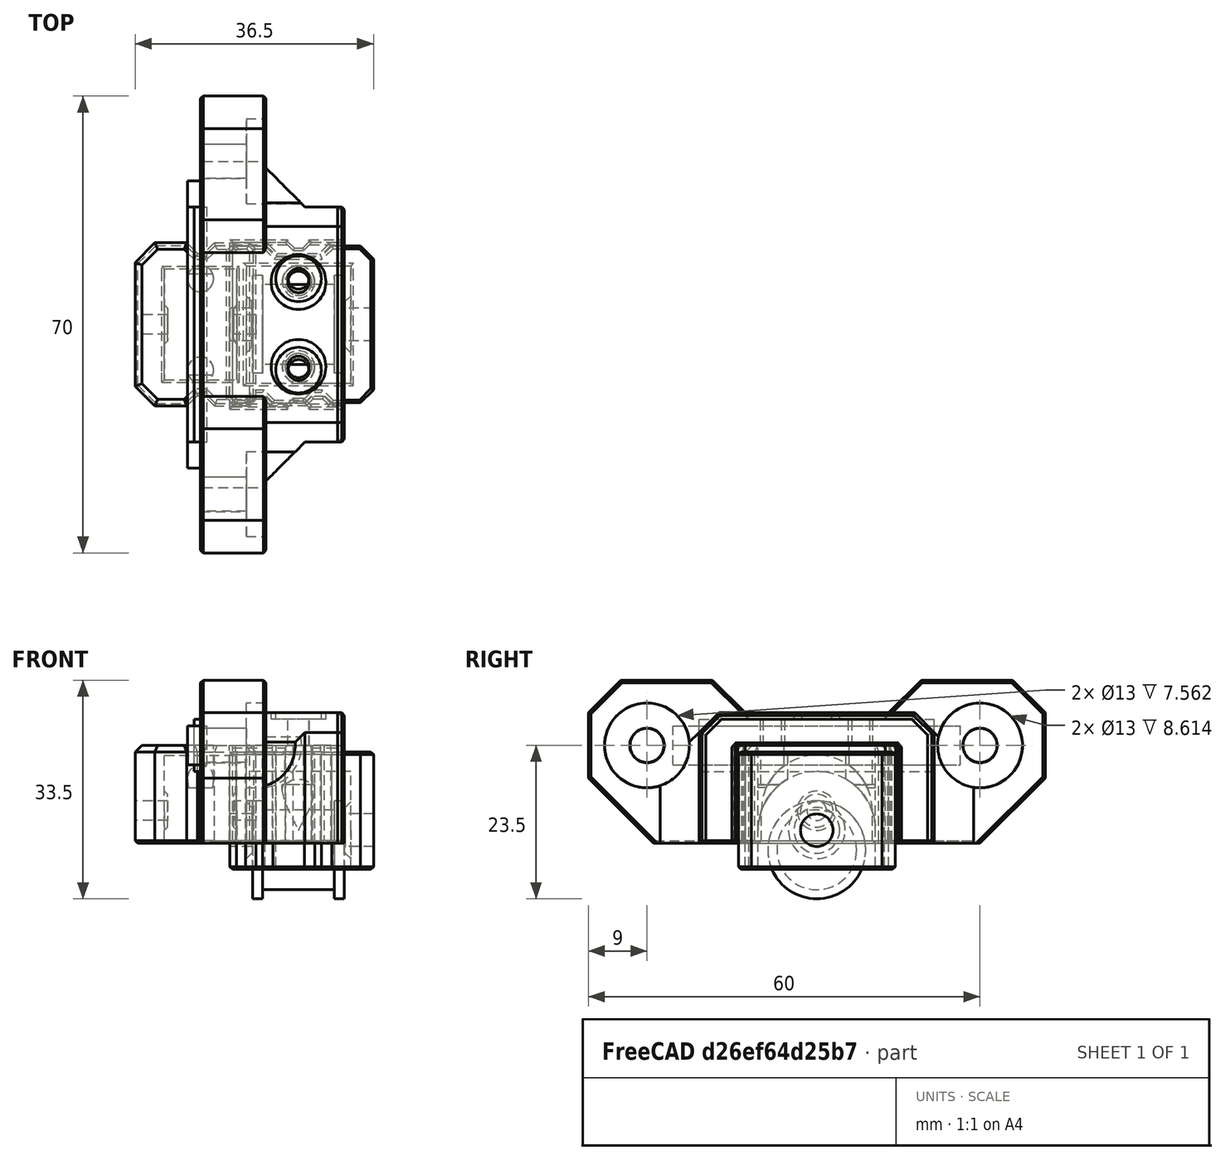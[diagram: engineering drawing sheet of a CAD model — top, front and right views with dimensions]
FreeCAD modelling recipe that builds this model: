
FCSTD DOCUMENT  (FreeCAD 0.18R16146 (Git))
Label: idler-tensioner-9mm
License: All rights reserved
LicenseURL: http://en.wikipedia.org/wiki/All_rights_reserved
objects: Part::Chamfer×38, Part::MultiFuse×33, Part::Cylinder×29, Part::Box×26, Part::Cut×12, Part::Feature×2, App::Part×2
note: 140 computed .brp shape members not serialized (recipe doc carries the construction recipe); baked Part::Feature solids carry a one-line shape summary decoded from their .brp

FEATURE [Part::Box] Box  label="Cube"
  AttacherType = Attacher::AttachEngine3D
  Height = 15
  Length = 18.5
  Placement = pos=(-10,-12.5,0) rot=(0,0,1;0rad)
  Width = 25
FEATURE [Part::Cylinder] Cylinder
  Angle = 360
  AttacherType = Attacher::AttachEngine3D
  Height = 22
  Placement = pos=(11,0,5) rot=(0,-1,0;1.5708rad)
  Radius = 1.5
FEATURE [Part::Cylinder] Cylinder001
  Angle = 360
  AttacherType = Attacher::AttachEngine3D
  Height = 11.1
  Placement = pos=(-5.55,0,5) rot=(0,1,0;1.5708rad)
  Radius = 8.5
FEATURE [Part::Box] Box001  label="Cube001"
  AttacherType = Attacher::AttachEngine3D
  Height = 5
  Length = 11.1
  Placement = pos=(-5.55,-8.5,0) rot=(0,0,1;0rad)
  Width = 17
FEATURE [Part::Cylinder] Cylinder003
  Angle = 360
  AttacherType = Attacher::AttachEngine3D
  Height = 10
  Placement = pos=(0,-7,8.5) rot=(0,0,1;0rad)
  Radius = 2
FEATURE [Part::Box] Box002  label="Cube002"
  AttacherType = Attacher::AttachEngine3D
  Height = 21
  Length = 4.2
  Placement = pos=(-2.1,-21,0) rot=(0,0,1;0rad)
  Width = 10.1
FEATURE [Part::Box] Box003  label="Cube003"
  AttacherType = Attacher::AttachEngine3D
  Height = 21
  Length = 4.2
  Placement = pos=(-2.1,10.9,0) rot=(0,0,1;0rad)
  Width = 10.1
FEATURE [Part::Cylinder] Cylinder004
  Angle = 360
  AttacherType = Attacher::AttachEngine3D
  Height = 1
  Placement = pos=(5.05,0,5) rot=(0,1,0;1.5708rad)
  Radius = 3
FEATURE [Part::Cylinder] Cylinder005
  Angle = 360
  AttacherType = Attacher::AttachEngine3D
  Height = 1
  Placement = pos=(-6.05,0,5) rot=(0,1,0;1.5708rad)
  Radius = 3
FEATURE [Part::Box] Box004  label="Cube004"
  AttacherType = Attacher::AttachEngine3D
  Height = 20
  Length = 22
  Placement = pos=(-15,-18,0) rot=(0,0,1;0rad)
  Width = 36
FEATURE [Part::Box] Box005  label="Cube005"
  AttacherType = Attacher::AttachEngine3D
  Height = 15
  Length = 20.2
  Placement = pos=(-10.1,-12.6,0) rot=(0,0,1;0rad)
  Width = 25.2
FEATURE [Part::Box] Box006  label="Cube006"
  AttacherType = Attacher::AttachEngine3D
  Height = 15
  Length = 4
  Placement = pos=(-2,11.3,0) rot=(0,0,1;0rad)
  Width = 1.7
FEATURE [Part::Box] Box007  label="Cube007"
  AttacherType = Attacher::AttachEngine3D
  Height = 15
  Length = 4
  Placement = pos=(-2,-13,0) rot=(0,0,1;0rad)
  Width = 1.7
FEATURE [Part::Cylinder] Cylinder006
  Angle = 360
  AttacherType = Attacher::AttachEngine3D
  Height = 10
  Placement = pos=(0,0,29) rot=(0,0,1;0rad)
  Radius = 3.5
FEATURE [Part::Cylinder] Cylinder007
  Angle = 360
  AttacherType = Attacher::AttachEngine3D
  Height = 12
  Placement = pos=(0,0,19) rot=(0,0,1;0rad)
  Radius = 1.6
FEATURE [Part::Box] Box008  label="Cube008"
  AttacherType = Attacher::AttachEngine3D
  Height = 6
  Length = 3
  Placement = pos=(-17,-22,12) rot=(0,0,1;0rad)
  Width = 44
FEATURE [Part::MultiFuse] Fusion
  Shapes = -> [Cylinder001,Box001]
FEATURE [Part::Chamfer] Chamfer003008
  Base = -> Box002
  Edges = 2 edges r=1.6: [Edge3,Edge7]
FEATURE [Part::Chamfer] Chamfer003009
  Base = -> Box003
  Edges = 2 edges r=1.6: [Edge1,Edge5]
FEATURE [Part::Cut] Cut
  Base = -> Box
  Tool = -> Fusion
FEATURE [Part::Cylinder] Cylinder008
  Angle = 360
  AttacherType = Attacher::AttachEngine3D
  Height = 10
  Placement = pos=(0,7,8.5) rot=(0,0,1;0rad)
  Radius = 2
FEATURE [Part::MultiFuse] Fusion007
  Shapes = -> [Cylinder003,Cylinder008]
FEATURE [Part::Cut] Cut001001009
  Base = -> Cut
  Tool = -> Fusion007
FEATURE [Part::MultiFuse] Fusion008
  Shapes = -> [Chamfer003008,Chamfer003009]
FEATURE [Part::Cut] Cut001001010
  Base = -> Cut001001009
  Tool = -> Fusion008
FEATURE [Part::Chamfer] Chamfer003010
  Base = -> Cut001001010
  Edges = 2 edges r=3: [Edge1,Edge3]
FEATURE [Part::Chamfer] Chamfer003011
  Base = -> Chamfer003010
  Edges = 2 edges r=1: [Edge48,Edge50]
FEATURE [Part::Chamfer] Chamfer003012
  Base = -> Chamfer003011
  Edges = 16 edges r=1: [Edge1,Edge2,Edge3,Edge4,Edge5,Edge6,Edge7,Edge8,Edge9,Edge10,Edge11,Edge12,Edge13,Edge14,Edge15,Edge16]
FEATURE [Part::Chamfer] Chamfer003015
  Base = -> Chamfer003012
  Edges = 24 edges r=0.4: [Edge60,Edge63,Edge64,Edge66,Edge69,Edge70,Edge72,Edge75,Edge76,Edge79,Edge81,Edge83,Edge84,Edge86,Edge88,Edge90,Edge97,Edge98,Edge99,Edge100,Edge101,Edge102,Edge103,Edge104]
FEATURE [Part::MultiFuse] Fusion011
  Shapes = -> [Box007,Box006]
FEATURE [Part::Chamfer] Chamfer
  Base = -> Fusion011
  Edges = 4 edges r=1.2: [Edge3,Edge7,Edge13,Edge17]
FEATURE [Part::MultiFuse] Fusion013
  Placement = pos=(0,-7,-10) rot=(0,0,1;0rad)
  Shapes = -> [Cylinder006,Cylinder007]
FEATURE [Part::Feature] Fusion013001  label="Fusion014"
  Placement = pos=(0,7,-10) rot=(0,0,1;0rad)
  shape: bbox 7 x 7 x 20 mm, 5 faces (baked)
FEATURE [Part::MultiFuse] Fusion013002
  Shapes = -> [Fusion013001,Fusion013]
FEATURE [Part::Box] Box009  label="Cube009"
  AttacherType = Attacher::AttachEngine3D
  Height = 25
  Length = 10
  Placement = pos=(-15,-35,0) rot=(0,0,1;0rad)
  Width = 24
FEATURE [Part::Box] Box010  label="Cube010"
  AttacherType = Attacher::AttachEngine3D
  Height = 25
  Length = 10
  Placement = pos=(-15,11,0) rot=(0,0,1;0rad)
  Width = 24
FEATURE [Part::MultiFuse] Fusion013004
  Shapes = -> [Box009,Box010]
FEATURE [Part::Cylinder] Cylinder009
  Angle = 360
  AttacherType = Attacher::AttachEngine3D
  Height = 10
  Radius = 2.6
FEATURE [Part::Cylinder] Cylinder010
  Angle = 360
  AttacherType = Attacher::AttachEngine3D
  Height = 10
  Placement = pos=(0,0,-10) rot=(0,0,1;0rad)
  Radius = 6.5
FEATURE [Part::Chamfer] Chamfer003021
  Base = -> Box004
  Edges = 2 edges r=3: [Edge10,Edge12]
FEATURE [Part::Chamfer] Chamfer003022
  Base = -> Chamfer003021
  Edges = 5 edges r=1: [Edge7,Edge11,Edge15,Edge16,Edge18]
FEATURE [Part::Chamfer] Chamfer003024
  Base = -> Chamfer003022
  Edges = 6 edges r=0.4: [Edge3,Edge6,Edge11,Edge12,Edge13,Edge14]
FEATURE [Part::Chamfer] Chamfer003027
  Base = -> Chamfer
  Edges = 10 edges r=0.4: [Edge4,Edge10,Edge14,Edge15,Edge16,Edge22,Edge28,Edge32,Edge33,Edge34]
FEATURE [Part::MultiFuse] Fusion013005006
  Shapes = -> [Cylinder005,Cylinder004]
FEATURE [Part::Chamfer] Chamfer003028
  Base = -> Fusion013005006
  Edges = 2 edges r=0.5: [Edge1,Edge6]
FEATURE [Part::MultiFuse] Fusion013005007
  Shapes = -> [Chamfer003028,Chamfer003015]
FEATURE [Part::Cut] Cut001001017
  Base = -> Fusion013005007
  Tool = -> Cylinder
FEATURE [App::Part] Part001  label="idler-inner"
  Group = -> [Box001,Cylinder004,Cut001001009,Box003,Chamfer003015,Box002,Box,Fusion,Cylinder005,Chamfer003009,Cylinder008,Cylinder001,Fusion007,Cylinder,Cut001001010,Cylinder003,Chamfer003010,Chamfer003012,Fusion008,Chamfer003011,Chamfer003008,Cut,Fusion013005006,Fusion013005007,Chamfer003028,Cut001001017]
  Origin = -> Origin001
  Placement = pos=(0,0,-4) rot=(0,0,1;0rad)
FEATURE [Part::Chamfer] Chamfer003029
  Base = -> Fusion013004
  Edges = 2 edges r=5: [Edge12,Edge22]
FEATURE [Part::Chamfer] Chamfer003030
  Base = -> Chamfer003029
  Edges = 2 edges r=5: [Edge7,Edge28]
FEATURE [Part::Chamfer] Chamfer003031
  Base = -> Chamfer003030
  Edges = 2 edges r=10: [Edge15,Edge33]
FEATURE [Part::Chamfer] Chamfer003032
  Base = -> Chamfer003031
  Edges = 22 edges r=0.4: [Edge1,Edge2,Edge3,Edge4,Edge5,Edge7,Edge8,Edge12,Edge14,Edge18,Edge21,Edge22,Edge23,Edge24,Edge25,Edge26,Edge28,Edge29,Edge33,Edge35,Edge39,Edge42]
FEATURE [Part::MultiFuse] Fusion013005008
  Shapes = -> [Chamfer003032,Chamfer003024]
FEATURE [Part::Chamfer] Chamfer003033
  Base = -> Fusion013005008
  Edges = 2 edges r=6: [Edge87,Edge89]
FEATURE [Part::Cut] Cut001001018
  Base = -> Chamfer003033
  Tool = -> Box005
FEATURE [Part::Chamfer] Chamfer003034
  Base = -> Cut001001018
  Edges = 2 edges r=0.4: [Edge64,Edge119]
FEATURE [Part::Chamfer] Chamfer003035
  Base = -> Chamfer003034
  Edges = 12 edges r=0.4: [Edge1,Edge2,Edge4,Edge6,Edge8,Edge14,Edge16,Edge31,Edge33,Edge44,Edge45,Edge46]
FEATURE [Part::MultiFuse] Fusion013005009
  Shapes = -> [Chamfer003035,Chamfer003027]
FEATURE [Part::Cut] Cut001001019
  Base = -> Fusion013005009
  Tool = -> Fusion013002
FEATURE [Part::MultiFuse] Fusion013005010
  Shapes = -> [Box008,Cut001001019]
FEATURE [Part::MultiFuse] Fusion013005011
  Placement = pos=(-8,-26,15) rot=(0,-1,0;1.5708rad)
  Shapes = -> [Cylinder009,Cylinder010]
FEATURE [Part::Feature] Fusion013005011001  label="Fusion013005012"
  Placement = pos=(-8,25,15) rot=(0,-1,0;1.5708rad)
  shape: bbox 20 x 13 x 13 mm, 5 faces (baked)
FEATURE [Part::MultiFuse] Fusion013005011002
  Shapes = -> [Fusion013005011001,Fusion013005011]
FEATURE [Part::Cut] Cut001001020
  Base = -> Fusion013005010
  Placement = pos=(15,0,0) rot=(0,0,1;0rad)
  Tool = -> Fusion013005011002
FEATURE [App::Part] Part  label="idler-outer"
  Group = -> [Box010,Box004,Fusion013004,Chamfer003027,Box006,Box008,Chamfer003024,Box007,Box005,Cylinder007,Cylinder006,Box009,Fusion013001,Cylinder010,Fusion011,Chamfer,Chamfer003021,Fusion013,Fusion013002,Cylinder009,Chamfer003022,Cut001001018,Chamfer003033,Fusion013005008,Chamfer003029,Chamfer003030,Chamfer003031,Chamfer003032,Fusion013005009,Fusion013005011002,Fusion013005010,Chamfer003035,Chamfer003034,+4 more]
  Origin = -> Origin
FEATURE [Part::Cylinder] Cylinder011
  Angle = 360
  AttacherType = Attacher::AttachEngine3D
  Height = 11
  Placement = pos=(5.5,0,1e-15) rot=(0,-1,0;1.5708rad)
  Radius = 6.11
FEATURE [Part::Cylinder] Cylinder012
  Angle = 360
  AttacherType = Attacher::AttachEngine3D
  Height = 1.5
  Placement = pos=(-5.5,0,3e-15) rot=(0,-1,0;1.5708rad)
  Radius = 7.5
FEATURE [Part::Cylinder] Cylinder013
  Angle = 360
  AttacherType = Attacher::AttachEngine3D
  Height = 1.5
  Placement = pos=(7,0,1e-15) rot=(0,-1,0;1.5708rad)
  Radius = 7.5
FEATURE [Part::MultiFuse] Fusion013005011003  label="20t-9mm-pulley"
  Placement = pos=(15,0,-1) rot=(0,0,1;0rad)
  Shapes = -> [Cylinder013,Cylinder012,Cylinder011]
FEATURE [Part::Box] Box011  label="Cube011"
  AttacherType = Attacher::AttachEngine3D
  Height = 6
  Length = 16
  Placement = pos=(7,-9,0) rot=(0,0,1;0rad)
  Width = 18
FEATURE [Part::Cylinder] Cylinder014
  Angle = 360
  AttacherType = Attacher::AttachEngine3D
  Height = 16
  Placement = pos=(23,0,6) rot=(0,-1,0;1.5708rad)
  Radius = 9
FEATURE [Part::Cylinder] Cylinder015
  Angle = 360
  AttacherType = Attacher::AttachEngine3D
  Height = 33
  Placement = pos=(31,0,6) rot=(0,-1,0;1.5708rad)
  Radius = 2.5
FEATURE [Part::MultiFuse] Fusion013005011004
  Shapes = -> [Cylinder014,Box011]
FEATURE [Part::Box] Box012  label="Cube012"
  AttacherType = Attacher::AttachEngine3D
  Height = 18
  Length = 22
  Placement = pos=(4.5,-12,0) rot=(0,0,1;0rad)
  Width = 24
FEATURE [Part::Cylinder] Cylinder016
  Angle = 360
  AttacherType = Attacher::AttachEngine3D
  Height = 1
  Placement = pos=(23.15,0,6) rot=(0,-1,0;1.5708rad)
  Radius = 4.35
FEATURE [Part::Cylinder] Cylinder017
  Angle = 360
  AttacherType = Attacher::AttachEngine3D
  Height = 1
  Placement = pos=(7.85,0,6) rot=(0,-1,0;1.5708rad)
  Radius = 4.35
FEATURE [Part::MultiFuse] Fusion013005011005
  Shapes = -> [Cylinder017,Cylinder016]
FEATURE [Part::Chamfer] Chamfer003036
  Base = -> Fusion013005011005
  Edges = 2 edges r=0.85: [Edge3,Edge4]
FEATURE [Part::Cut] Cut001001021
  Base = -> Box012
  Tool = -> Fusion013005011004
FEATURE [Part::MultiFuse] Fusion013005011006
  Shapes = -> [Chamfer003036,Cut001001021]
FEATURE [Part::Box] Box013  label="Cube013"
  AttacherType = Attacher::AttachEngine3D
  Height = 22
  Length = 10.2
  Placement = pos=(9.9,10.4,0) rot=(0,0,1;0rad)
  Width = 10
FEATURE [Part::Box] Box014  label="Cube014"
  AttacherType = Attacher::AttachEngine3D
  Height = 22
  Length = 4.2
  Placement = pos=(6.9,-20.4,0) rot=(0,0,1;0rad)
  Width = 10
FEATURE [Part::Box] Box015  label="Cube015"
  AttacherType = Attacher::AttachEngine3D
  Height = 18
  Length = 22.2
  Placement = pos=(4.4,-12.1,0) rot=(0,0,1;0rad)
  Width = 24.2
FEATURE [Part::Cylinder] Cylinder018
  Angle = 360
  AttacherType = Attacher::AttachEngine3D
  Height = 10
  Placement = pos=(15,-6.5,13) rot=(0,0,1;0rad)
  Radius = 2.05
FEATURE [Part::Cylinder] Cylinder019
  Angle = 360
  AttacherType = Attacher::AttachEngine3D
  Height = 10
  Placement = pos=(15,6.5,13) rot=(0,0,1;0rad)
  Radius = 2.05
FEATURE [Part::Cylinder] Cylinder020
  Angle = 360
  AttacherType = Attacher::AttachEngine3D
  Height = 10
  Placement = pos=(15,-6.5,3) rot=(0,0,1;0rad)
  Radius = 2.5
FEATURE [Part::Cylinder] Cylinder021
  Angle = 360
  AttacherType = Attacher::AttachEngine3D
  Height = 10
  Placement = pos=(15,6.5,3) rot=(0,0,1;0rad)
  Radius = 2.5
FEATURE [Part::MultiFuse] Fusion013005011008
  Shapes = -> [Cylinder018,Cylinder019]
FEATURE [Part::MultiFuse] Fusion013005011009
  Shapes = -> [Cylinder021,Cylinder020]
FEATURE [Part::MultiFuse] Fusion013005011010
  Shapes = -> [Fusion013005011009,Fusion013005011008]
FEATURE [Part::Chamfer] Chamfer003042
  Base = -> Box015
  Edges = 2 edges r=1: [Edge1,Edge3]
  Placement = pos=(0,0,-3) rot=(0,0,1;0rad)
FEATURE [Part::Box] Box018  label="Cube018"
  AttacherType = Attacher::AttachEngine3D
  Height = 20
  Length = 22
  Placement = pos=(0,-18,0) rot=(0,0,1;0rad)
  Width = 36
FEATURE [Part::Box] Box019  label="Cube019"
  AttacherType = Attacher::AttachEngine3D
  Height = 25
  Length = 10
  Placement = pos=(0,-35,0) rot=(0,0,1;0rad)
  Width = 24
FEATURE [Part::Box] Box020  label="Cube020"
  AttacherType = Attacher::AttachEngine3D
  Height = 25
  Length = 10
  Placement = pos=(0,11,0) rot=(0,0,1;0rad)
  Width = 24
FEATURE [Part::Chamfer] Chamfer003043
  Base = -> Box019
  Edges = 2 edges r=5: [Edge10,Edge12]
FEATURE [Part::Chamfer] Chamfer003044
  Base = -> Box020
  Edges = 2 edges r=5: [Edge10,Edge12]
FEATURE [Part::Chamfer] Chamfer003045
  Base = -> Chamfer003043
  Edges = 1 edges r=10: [Edge9]
FEATURE [Part::Chamfer] Chamfer003046
  Base = -> Chamfer003044
  Edges = 1 edges r=10: [Edge12]
FEATURE [Part::Chamfer] Chamfer003047
  Base = -> Chamfer003045
  Edges = 11 edges r=0.4: [Edge1,Edge2,Edge3,Edge4,Edge5,Edge7,Edge8,Edge12,Edge14,Edge18,Edge21]
FEATURE [Part::Chamfer] Chamfer003048
  Base = -> Chamfer003046
  Edges = 11 edges r=0.4: [Edge1,Edge2,Edge4,Edge5,Edge6,Edge7,Edge12,Edge15,Edge18,Edge20,Edge21]
FEATURE [Part::Chamfer] Chamfer003049
  Base = -> Box018
  Edges = 2 edges r=3: [Edge10,Edge12]
FEATURE [Part::Chamfer] Chamfer003050
  Base = -> Chamfer003049
  Edges = 8 edges r=0.4: [Edge3,Edge4,Edge7,Edge11,Edge13,Edge15,Edge16,Edge18]
FEATURE [Part::MultiFuse] Fusion013005011013
  Shapes = -> [Chamfer003047,Chamfer003050,Chamfer003048]
FEATURE [Part::Chamfer] Chamfer003051
  Base = -> Fusion013005011013
  Edges = 2 edges r=6: [Edge85,Edge87]
FEATURE [Part::Box] Box021  label="Cube021"
  AttacherType = Attacher::AttachEngine3D
  Height = 15
  Length = 10
  Placement = pos=(10,10.5,0) rot=(0,0,1;0rad)
  Width = 3
FEATURE [Part::Box] Box022  label="Cube022"
  AttacherType = Attacher::AttachEngine3D
  Height = 15
  Length = 4
  Placement = pos=(7,-13.5,0) rot=(0,0,1;0rad)
  Width = 3
FEATURE [Part::Cylinder] Cylinder022
  Angle = 360
  AttacherType = Attacher::AttachEngine3D
  Height = 1
  Placement = pos=(15,6.5,19) rot=(0,0,1;0rad)
  Radius = 4.2
FEATURE [Part::Cylinder] Cylinder023
  Angle = 360
  AttacherType = Attacher::AttachEngine3D
  Height = 1
  Placement = pos=(15,-6.5,19) rot=(0,0,1;0rad)
  Radius = 4.2
FEATURE [Part::Cylinder] Cylinder024
  Angle = 360
  AttacherType = Attacher::AttachEngine3D
  Height = 10
  Placement = pos=(15,6.5,12) rot=(0,0,1;0rad)
  Radius = 1.65
FEATURE [Part::Cylinder] Cylinder025
  Angle = 360
  AttacherType = Attacher::AttachEngine3D
  Height = 10
  Placement = pos=(15,-6.5,12) rot=(0,0,1;0rad)
  Radius = 1.65
FEATURE [Part::MultiFuse] Fusion013005011016
  Shapes = -> [Cylinder025,Cylinder024]
FEATURE [Part::MultiFuse] Fusion013005011017
  Shapes = -> [Cylinder023,Cylinder022]
FEATURE [Part::Cylinder] Cylinder026
  Angle = 360
  AttacherType = Attacher::AttachEngine3D
  Height = 10
  Placement = pos=(-3e-15,25,15) rot=(0,1,0;1.5708rad)
  Radius = 2.65
FEATURE [Part::Cylinder] Cylinder027
  Angle = 360
  AttacherType = Attacher::AttachEngine3D
  Height = 10
  Placement = pos=(-3e-15,-26,15) rot=(0,1,0;1.5708rad)
  Radius = 2.65
FEATURE [Part::Cylinder] Cylinder028
  Angle = 360
  AttacherType = Attacher::AttachEngine3D
  Height = 10
  Placement = pos=(-3e-15,-26,15) rot=(0,1,0;1.5708rad)
  Radius = 6.5
FEATURE [Part::Cylinder] Cylinder029
  Angle = 360
  AttacherType = Attacher::AttachEngine3D
  Height = 10
  Placement = pos=(-3e-15,25,15) rot=(0,1,0;1.5708rad)
  Radius = 6.5
FEATURE [Part::MultiFuse] Fusion013005011018
  Shapes = -> [Cylinder027,Cylinder026]
FEATURE [Part::MultiFuse] Fusion013005011019
  Placement = pos=(7,0,0) rot=(0,0,1;0rad)
  Shapes = -> [Cylinder029,Cylinder028]
FEATURE [Part::MultiFuse] Fusion013005011020
  Shapes = -> [Fusion013005011019,Fusion013005011018]
FEATURE [Part::Box] Box023  label="6mm-tap"
  AttacherType = Attacher::AttachEngine3D
  Height = 6
  Length = 3
  Placement = pos=(-2,-18,12) rot=(0,0,1;0rad)
  Width = 36
FEATURE [Part::Box] Box024  label="8mm-tap"
  AttacherType = Attacher::AttachEngine3D
  Height = 8
  Length = 1
  Placement = pos=(-1,-18,11) rot=(0,0,1;0rad)
  Width = 36
FEATURE [Part::Box] Box025  label="Cube023"
  AttacherType = Attacher::AttachEngine3D
  Height = 22
  Length = 4.2
  Placement = pos=(15.9,-20.4,0) rot=(0,0,1;0rad)
  Width = 10
FEATURE [Part::MultiFuse] Fusion013005011021
  Shapes = -> [Box014,Box013,Box025]
FEATURE [Part::Chamfer] Chamfer003055
  Base = -> Fusion013005011021
  Edges = 6 edges r=1.6: [Edge3,Edge7,Edge13,Edge17,Edge27,Edge31]
FEATURE [Part::MultiFuse] Fusion013005011022
  Shapes = -> [Chamfer003055,Fusion013005011010,Cylinder015]
FEATURE [Part::Cut] Cut001001029
  Base = -> Fusion013005011006
  Tool = -> Fusion013005011022
FEATURE [Part::Chamfer] Chamfer003056
  Base = -> Cut001001029
  Edges = 2 edges r=1: [Edge84,Edge113]
FEATURE [Part::Chamfer] Chamfer003057
  Base = -> Chamfer003056
  Edges = 2 edges r=2: [Edge45,Edge49]
FEATURE [Part::Chamfer] Chamfer003058
  Base = -> Chamfer003057
  Edges = 22 edges r=0.4: [Edge31,Edge33,Edge35,Edge36,Edge39,Edge42,Edge43,Edge46,Edge48,Edge50,Edge52,Edge53,Edge55,Edge58,Edge61,Edge62,Edge65,Edge67,Edge69,Edge70,Edge91,Edge92]
FEATURE [Part::Chamfer] Chamfer003059
  Base = -> Chamfer003058
  Edges = 28 edges r=0.4: [Edge3,Edge6,Edge11,Edge12,Edge13,Edge14,Edge15,Edge16,Edge17,Edge18,Edge19,Edge20,Edge21,Edge22,Edge23,Edge24,Edge25,Edge26,Edge27,Edge28,Edge29,Edge30,Edge31,Edge32,Edge33,Edge34,Edge35,Edge36]
  Placement = pos=(0,0,-4) rot=(0,0,1;0rad)
FEATURE [Part::MultiFuse] Fusion013005011023
  Shapes = -> [Fusion013005011020,Fusion013005011016]
FEATURE [Part::MultiFuse] Fusion013005011024
  Shapes = -> [Fusion013005011017,Fusion013005011023]
FEATURE [Part::Cut] Cut001001030
  Base = -> Chamfer003051
  Tool = -> Fusion013005011024
FEATURE [Part::Cut] Cut001001031
  Base = -> Cut001001030
  Tool = -> Chamfer003042
FEATURE [Part::Box] Box026  label="Cube024"
  AttacherType = Attacher::AttachEngine3D
  Height = 15
  Length = 4
  Placement = pos=(16,-13.5,0) rot=(0,0,1;0rad)
  Width = 3
FEATURE [Part::MultiFuse] Fusion013005011025
  Shapes = -> [Box026,Box021,Box022]
FEATURE [Part::Chamfer] Chamfer003060
  Base = -> Fusion013005011025
  Edges = 6 edges r=1.6: [Edge3,Edge7,Edge13,Edge17,Edge27,Edge31]
FEATURE [Part::Box] Box027  label="Cube025"
  AttacherType = Attacher::AttachEngine3D
  Height = 19
  Length = 13
  Placement = pos=(6,-11,0) rot=(0,0,1;0rad)
  Width = 10
FEATURE [Part::Cut] Cut001001032
  Base = -> Chamfer003060
  Tool = -> Box027
FEATURE [Part::Chamfer] Chamfer003061
  Base = -> Cut001001032
  Edges = 18 edges r=0.4: [Edge4,Edge10,Edge12,Edge14,Edge15,Edge16,Edge22,Edge28,Edge30,Edge32,Edge33,Edge34,Edge40,Edge46,Edge48,Edge50,Edge51,Edge52]
FEATURE [Part::Chamfer] Chamfer003062
  Base = -> Cut001001031
  Edges = 12 edges r=0.4: [Edge22,Edge28,Edge29,Edge63,Edge65,Edge70,Edge131,Edge132,Edge143,Edge144,Edge179,Edge181]
FEATURE [Part::MultiFuse] Fusion013005011026
  Shapes = -> [Chamfer003062,Chamfer003061]
